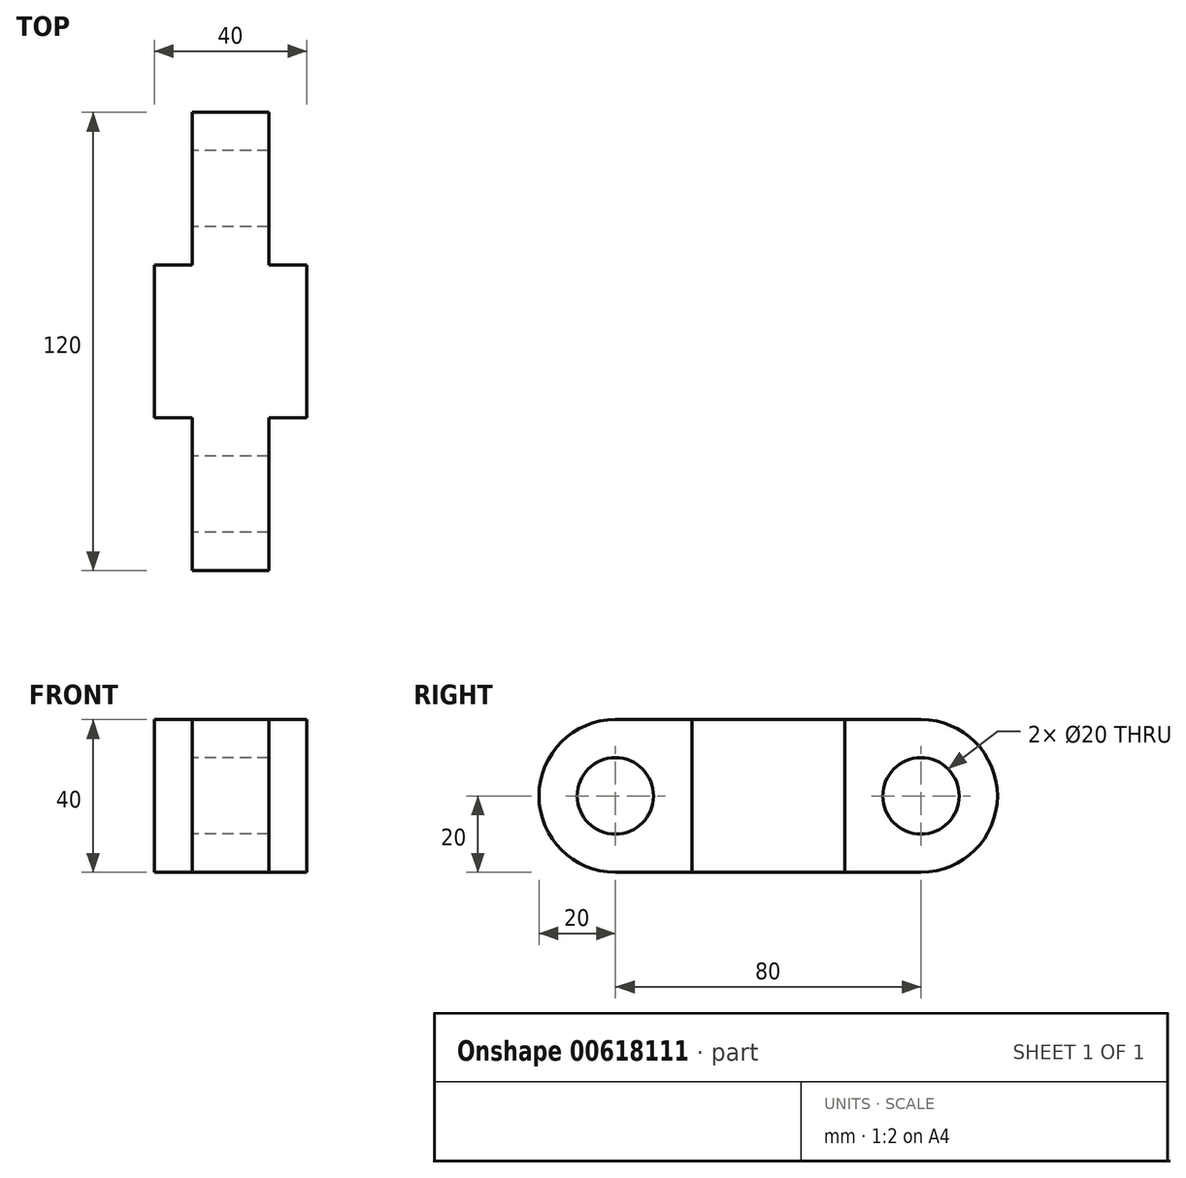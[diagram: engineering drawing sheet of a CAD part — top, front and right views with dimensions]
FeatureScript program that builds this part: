
annotation { "Feature Type Name" : "Feature", "Feature Type Description" : "" }
export const myFeature = defineFeature(function(context is Context, id is Id, definition is map)
    precondition{}
    {
        {
            var Q0;
            Q0=qCreatedBy(makeId("Top.planeOp"),FACE);
            var sketch = newSketch(context, id + "F0", { "sketchPlane" : qUnion([Q0])});
            skLineSegment(sketch, "E0.bottom", {"start": v(10, 0) * mm, "end": v(30, 0) * mm});
            skLineSegment(sketch, "E0.top", {"start": v(10, 120) * mm, "end": v(30, 120) * mm});
            skLineSegment(sketch, "E0.left", {"start": v(0, 40) * mm, "end": v(0, 80) * mm});
            skLineSegment(sketch, "E0.right", {"start": v(40, 40) * mm, "end": v(40, 80) * mm});
            skLineSegment(sketch, "E1.top", {"start": v(0, 40) * mm, "end": v(10, 40) * mm});
            skLineSegment(sketch, "E1.right", {"start": v(10, 0) * mm, "end": v(10, 40) * mm});
            skLineSegment(sketch, "E2.top", {"start": v(0, 80) * mm, "end": v(10, 80) * mm});
            skLineSegment(sketch, "E2.right", {"start": v(10, 120) * mm, "end": v(10, 80) * mm});
            skLineSegment(sketch, "E3.top", {"start": v(40, 80) * mm, "end": v(30, 80) * mm});
            skLineSegment(sketch, "E3.right", {"start": v(30, 120) * mm, "end": v(30, 80) * mm});
            skLineSegment(sketch, "E4.top", {"start": v(40, 40) * mm, "end": v(30, 40) * mm});
            skLineSegment(sketch, "E4.right", {"start": v(30, 0) * mm, "end": v(30, 40) * mm});
            skSolve(sketch);
        }
        {
            var Q0;
            Q0=makeQuery(id+"F0.imprint","IMPRINT",FACE,{"disambiguationData":[TD([[makeQuery(id+"F0.imprint","IMPRINT",EDGE,{"derivedFrom":sQuery(id+"F0.wireOp",EDGE,"E0.bottom")}),1.0]])]});
            extrude(context, id + "F1", {"entities" : qUnion([Q0]), "depth" : 40 * mm, "offsetDistance" : 25 * mm});
        }
        {
            var Q0;
            Q0=makeQuery(id+"F1.opExtrude","SWEPT_FACE",FACE,{"disambiguationData":[OSD([sQuery(id+"F0.wireOp",EDGE,"E2.right")])]});
            var sketch = newSketch(context, id + "F2", { "sketchPlane" : qUnion([Q0])});
            skCircle(sketch, "E5", {"center": v(-100, 20) * mm, "radius": 10 * mm});
            skPoint(sketch, "E6.orphan", {"position": v(-100, 40) * mm});
            skPoint(sketch, "E7.trimOffspring.end.orphan", {"position": v(-80, 20) * mm});
            skPoint(sketch, "E8.start.orphan", {"position": v(-120, 20) * mm});
            skPoint(sketch, "E9.start.orphan", {"position": v(-100, 0) * mm});
            skSolve(sketch);
        }
        {
            var Q0;
            Q0=makeQuery(id+"F2.imprint","IMPRINT",FACE,{"disambiguationData":[TD([[makeQuery(id+"F2.imprint","IMPRINT",EDGE,{"derivedFrom":sQuery(id+"F2.wireOp",EDGE,"E5")}),1.0]])]});
            extrude(context, id + "F3", {"entities" : qUnion([Q0]), "operationType" : NewBodyOperationType.REMOVE, "oppositeDirection" : true, "depth" : 20 * mm, "offsetDistance" : 25 * mm});
        }
        {
            var Q0;
            Q0=makeQuery(id+"F1.opExtrude","SWEPT_FACE",FACE,{"disambiguationData":[OSD([sQuery(id+"F0.wireOp",EDGE,"E1.right")])]});
            var sketch = newSketch(context, id + "F4", { "sketchPlane" : qUnion([Q0])});
            skCircle(sketch, "E10", {"center": v(-20, 20) * mm, "radius": 10 * mm});
            skPoint(sketch, "E11.orphan", {"position": v(-20, 40) * mm});
            skPoint(sketch, "E12.orphan", {"position": v(0, 20) * mm});
            skPoint(sketch, "E13.end.orphan", {"position": v(-20, 0) * mm});
            skPoint(sketch, "E14.start.orphan", {"position": v(-40, 20) * mm});
            skSolve(sketch);
        }
        {
            var Q0;
            Q0=makeQuery(id+"F4.imprint","IMPRINT",FACE,{"disambiguationData":[TD([[makeQuery(id+"F4.imprint","IMPRINT",EDGE,{"derivedFrom":sQuery(id+"F4.wireOp",EDGE,"E10")}),1.0]])]});
            extrude(context, id + "F5", {"entities" : qUnion([Q0]), "operationType" : NewBodyOperationType.REMOVE, "oppositeDirection" : true, "depth" : 20 * mm, "offsetDistance" : 25 * mm});
        }
        {
            var Q0;
            Q0=makeQuery(id+"F1.opExtrude","CAP_EDGE",EDGE,{"disambiguationData":[OSD([sQuery(id+"F0.wireOp",EDGE,"E0.bottom")])],"isStart":false});
            fillet(context, id + "F6", {"entities" : qUnion([Q0]), "radius" : 20 * mm, "tangentPropagation" : true, "allowEdgeOverflow" : false});
        }
        {
            var Q0;
            Q0=makeQuery(id+"F1.opExtrude","CAP_EDGE",EDGE,{"disambiguationData":[OSD([sQuery(id+"F0.wireOp",EDGE,"E0.bottom")])],"isStart":true});
            fillet(context, id + "F7", {"entities" : qUnion([Q0]), "radius" : 20 * mm, "tangentPropagation" : true, "allowEdgeOverflow" : false});
        }
        {
            var Q0;
            Q0=makeQuery(id+"F1.opExtrude","CAP_EDGE",EDGE,{"disambiguationData":[OSD([sQuery(id+"F0.wireOp",EDGE,"E0.top")])],"isStart":false});
            fillet(context, id + "F8", {"entities" : qUnion([Q0]), "radius" : 20 * mm, "tangentPropagation" : true, "allowEdgeOverflow" : false});
        }
        {
            var Q0;
            Q0=makeQuery(id+"F1.opExtrude","CAP_EDGE",EDGE,{"disambiguationData":[OSD([sQuery(id+"F0.wireOp",EDGE,"E0.top")])],"isStart":true});
            fillet(context, id + "F9", {"entities" : qUnion([Q0]), "radius" : 20 * mm, "tangentPropagation" : true, "allowEdgeOverflow" : false});
        }
    });
